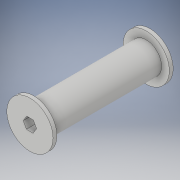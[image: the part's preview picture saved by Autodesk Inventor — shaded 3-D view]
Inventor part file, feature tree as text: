
AUTODESK INVENTOR PART (.ipt)
format: ipt  version: 2018 (Build 220112000, 112)  size: 138,752 bytes
history: native  units: in
note: dims shown in document units (in); Inventor stores cm internally (conversion verified against a paired STEP export)
features: extrude x3, sketch x3
ambient origin geometry x8: Origin, YZ Plane, XZ Plane, XY Plane, X Axis, Y Axis, Z Axis, Center Point
bodies: Solid1 (feature_tree)
feature tree (6):
  extrude  "Extrusion1"  Depth=0.375in
  extrude  "Extrusion2"  Depth=3.65in
  extrude  "Extrusion3"  Depth=0.5in
  sketch  "Sketch1"  dims[d0=0.375in d1=1.0in]
  sketch  "Sketch3"  dims[d2=3.65in d3=0.0in d4=1.5in]
  sketch  "Sketch4"  dims[d5=0.125in d6=0.0in d7=0.5in d8=180.0deg d9=0.125in d10=0.0in d11=1.5in]
